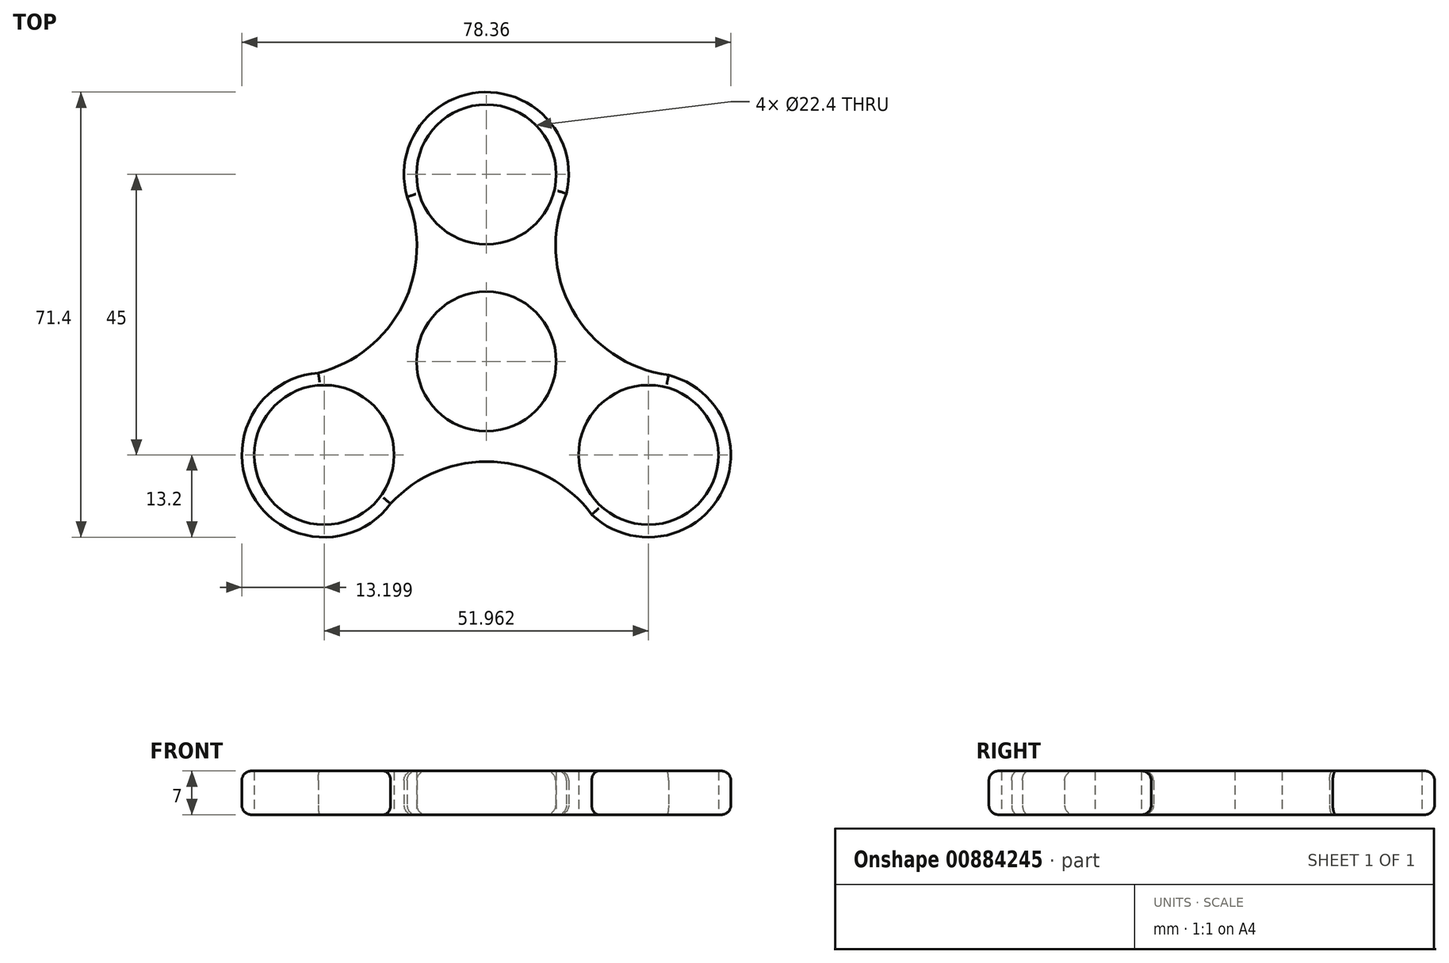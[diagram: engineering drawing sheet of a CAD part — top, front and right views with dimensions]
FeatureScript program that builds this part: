
annotation { "Feature Type Name" : "Feature", "Feature Type Description" : "" }
export const myFeature = defineFeature(function(context is Context, id is Id, definition is map)
    precondition{}
    {
        {
            var Q0;
            Q0=qCreatedBy(makeId("Top.planeOp"),FACE);
            var sketch = newSketch(context, id + "F0", { "sketchPlane" : qUnion([Q0])});
            skCircle(sketch, "E0", {"center": v(0, 0) * mm, "radius": 11.2 * mm});
            skCircle(sketch, "E1", {"center": v(0, 30) * mm, "radius": 11.2 * mm});
            skArc(sketch, "E2", {"start": v(12.83, 26.9) * mm, "mid": v(-0.27, 43.2) * mm, "end": v(-12.7, 26.38) * mm});
            skArc(sketch, "E3.1.0", {"start": v(-26.94, -1.83) * mm, "mid": v(-37.53, -21.38) * mm, "end": v(-15.35, -22.82) * mm});
            skCircle(sketch, "E3.1.1", {"center": v(-25.98, -15) * mm, "radius": 11.2 * mm});
            skArc(sketch, "E3.2.0", {"start": v(16.89, -24.57) * mm, "mid": v(37.55, -21.36) * mm, "end": v(29.2, -2.2) * mm});
            skCircle(sketch, "E3.2.1", {"center": v(25.98, -15) * mm, "radius": 11.2 * mm});
            skLineSegment(sketch, "E4", {"start": v(0, 30) * mm, "end": v(25.98, -15) * mm, "construction": true});
            skLineSegment(sketch, "E5", {"start": v(-25.98, -15) * mm, "end": v(0, 0) * mm, "construction": true});
            skLineSegment(sketch, "E6", {"start": v(0, 0) * mm, "end": v(29.2, 16.85) * mm, "construction": true});
            skLineSegment(sketch, "E7", {"start": v(12.83, 26.9) * mm, "end": v(29.2, -2.2) * mm, "construction": true});
            skArc(sketch, "E8", {"start": v(12.83, 26.9) * mm, "mid": v(13.77, 8.29) * mm, "end": v(29.2, -2.2) * mm});
            skArc(sketch, "E9.1.0", {"start": v(-26.94, -1.83) * mm, "mid": v(-13.38, 9.02) * mm, "end": v(-12.7, 26.38) * mm});
            skArc(sketch, "E9.2.0", {"start": v(16.89, -24.57) * mm, "mid": v(1.18, -16.1) * mm, "end": v(-15.35, -22.82) * mm});
            skPoint(sketch, "E10.orphan", {"position": v(-16.5, -24.18) * mm});
            skPoint(sketch, "E11.orphan", {"position": v(-29.72, -2.34) * mm});
            skSolve(sketch);
        }
        {
            var Q0;
            Q0=makeQuery(id+"F0.imprint","IMPRINT",FACE,{"disambiguationData":[TD([[makeQuery(id+"F0.imprint","IMPRINT",EDGE,{"derivedFrom":sQuery(id+"F0.wireOp",EDGE,"E0")}),-1.0]])]});
            extrude(context, id + "F1", {"entities" : qUnion([Q0]), "depth" : 7 * mm, "offsetDistance" : 25 * mm});
        }
        {
            var Q0;
            Q0=makeQuery(id+"F1.opExtrude","CAP_EDGE",EDGE,{"disambiguationData":[OSD([sQuery(id+"F0.wireOp",EDGE,"E8")])],"isStart":false});
            var Q1;
            Q1=makeQuery(id+"F1.opExtrude","CAP_EDGE",EDGE,{"disambiguationData":[OSD([sQuery(id+"F0.wireOp",EDGE,"E2")])],"isStart":false});
            var Q2;
            Q2=makeQuery(id+"F1.opExtrude","CAP_EDGE",EDGE,{"disambiguationData":[OSD([sQuery(id+"F0.wireOp",EDGE,"E9.1.0")])],"isStart":false});
            var Q3;
            Q3=makeQuery(id+"F1.opExtrude","CAP_EDGE",EDGE,{"disambiguationData":[OSD([sQuery(id+"F0.wireOp",EDGE,"E3.1.0")])],"isStart":false});
            var Q4;
            Q4=makeQuery(id+"F1.opExtrude","CAP_EDGE",EDGE,{"disambiguationData":[OSD([sQuery(id+"F0.wireOp",EDGE,"E9.2.0")])],"isStart":false});
            var Q5;
            Q5=makeQuery(id+"F1.opExtrude","CAP_EDGE",EDGE,{"disambiguationData":[OSD([sQuery(id+"F0.wireOp",EDGE,"E3.2.0")])],"isStart":false});
            var Q6;
            Q6=makeQuery(id+"F1.opExtrude","CAP_EDGE",EDGE,{"disambiguationData":[OSD([sQuery(id+"F0.wireOp",EDGE,"E8")])],"isStart":true});
            var Q7;
            Q7=makeQuery(id+"F1.opExtrude","CAP_EDGE",EDGE,{"disambiguationData":[OSD([sQuery(id+"F0.wireOp",EDGE,"E2")])],"isStart":true});
            var Q8;
            Q8=makeQuery(id+"F1.opExtrude","CAP_EDGE",EDGE,{"disambiguationData":[OSD([sQuery(id+"F0.wireOp",EDGE,"E9.1.0")])],"isStart":true});
            var Q9;
            Q9=makeQuery(id+"F1.opExtrude","CAP_EDGE",EDGE,{"disambiguationData":[OSD([sQuery(id+"F0.wireOp",EDGE,"E3.1.0")])],"isStart":true});
            var Q10;
            Q10=makeQuery(id+"F1.opExtrude","CAP_EDGE",EDGE,{"disambiguationData":[OSD([sQuery(id+"F0.wireOp",EDGE,"E9.2.0")])],"isStart":true});
            var Q11;
            Q11=makeQuery(id+"F1.opExtrude","CAP_EDGE",EDGE,{"disambiguationData":[OSD([sQuery(id+"F0.wireOp",EDGE,"E3.2.0")])],"isStart":true});
            fillet(context, id + "F2", {"entities" : qUnion([Q0, Q1, Q2, Q3, Q4, Q5, Q6, Q7, Q8, Q9, Q10, Q11]), "radius" : 1.5 * mm, "tangentPropagation" : true, "allowEdgeOverflow" : false});
        }
    });
